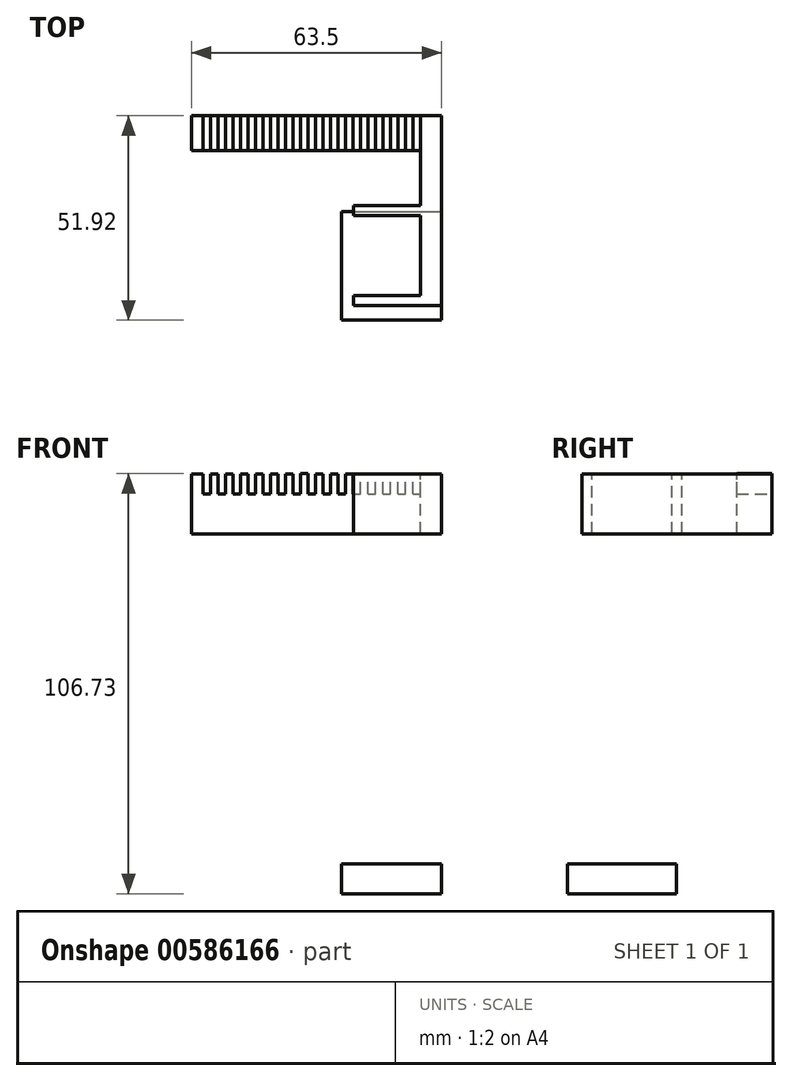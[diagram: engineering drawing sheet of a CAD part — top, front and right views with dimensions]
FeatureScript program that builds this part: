
annotation { "Feature Type Name" : "Feature", "Feature Type Description" : "" }
export const myFeature = defineFeature(function(context is Context, id is Id, definition is map)
    precondition{}
    {
        {
            var Q0;
            Q0=qCreatedBy(makeId("Front.planeOp"),FACE);
            var sketch = newSketch(context, id + "F0", { "sketchPlane" : qUnion([Q0])});
            skLineSegment(sketch, "E0.bottom", {"start": v(-64.89, 15.49) * mm, "end": v(-1.39, 15.49) * mm});
            skLineSegment(sketch, "E0.top", {"start": v(-64.89, 5.33) * mm, "end": v(-1.39, 5.33) * mm});
            skLineSegment(sketch, "E0.left", {"start": v(-64.89, 15.49) * mm, "end": v(-64.89, 5.33) * mm});
            skLineSegment(sketch, "E0.right", {"start": v(-1.39, 15.49) * mm, "end": v(-1.39, 5.33) * mm});
            skLineSegment(sketch, "E1.bottom", {"start": v(-1.39, 15.49) * mm, "end": v(-13.31, 15.49) * mm});
            skLineSegment(sketch, "E1.top", {"start": v(-11.73, 20.57) * mm, "end": v(-13.31, 20.57) * mm});
            skLineSegment(sketch, "E2.bottom", {"start": v(-48.7, 15.49) * mm, "end": v(-46.79, 15.49) * mm});
            skLineSegment(sketch, "E2.top", {"start": v(-48.7, 20.57) * mm, "end": v(-46.79, 20.57) * mm});
            skLineSegment(sketch, "E2.left", {"start": v(-48.7, 15.49) * mm, "end": v(-48.7, 20.57) * mm});
            skLineSegment(sketch, "E2.right", {"start": v(-46.79, 15.49) * mm, "end": v(-46.79, 20.57) * mm});
            skLineSegment(sketch, "E3.bottom", {"start": v(-44.88, 15.49) * mm, "end": v(-42.98, 15.49) * mm});
            skLineSegment(sketch, "E3.top", {"start": v(-44.88, 20.57) * mm, "end": v(-42.98, 20.57) * mm});
            skLineSegment(sketch, "E3.left", {"start": v(-44.88, 15.49) * mm, "end": v(-44.88, 20.57) * mm});
            skLineSegment(sketch, "E3.right", {"start": v(-42.98, 15.49) * mm, "end": v(-42.98, 20.57) * mm});
            skLineSegment(sketch, "E4.bottom", {"start": v(-41.07, 15.49) * mm, "end": v(-39.17, 15.49) * mm});
            skLineSegment(sketch, "E4.top", {"start": v(-41.07, 20.57) * mm, "end": v(-39.17, 20.57) * mm});
            skLineSegment(sketch, "E4.left", {"start": v(-41.07, 15.49) * mm, "end": v(-41.07, 20.57) * mm});
            skLineSegment(sketch, "E4.right", {"start": v(-39.17, 15.49) * mm, "end": v(-39.17, 20.57) * mm});
            skLineSegment(sketch, "E5.bottom", {"start": v(-37.26, 15.49) * mm, "end": v(-35.36, 15.49) * mm});
            skLineSegment(sketch, "E5.top", {"start": v(-37.26, 20.62) * mm, "end": v(-35.36, 20.62) * mm});
            skLineSegment(sketch, "E5.left", {"start": v(-37.26, 15.49) * mm, "end": v(-37.26, 20.62) * mm});
            skLineSegment(sketch, "E5.right", {"start": v(-35.36, 15.49) * mm, "end": v(-35.36, 20.62) * mm});
            skLineSegment(sketch, "E6.bottom", {"start": v(-33.45, 15.49) * mm, "end": v(-31.55, 15.49) * mm});
            skLineSegment(sketch, "E6.top", {"start": v(-33.45, 20.57) * mm, "end": v(-31.55, 20.57) * mm});
            skLineSegment(sketch, "E6.left", {"start": v(-33.45, 15.49) * mm, "end": v(-33.45, 20.57) * mm});
            skLineSegment(sketch, "E6.right", {"start": v(-31.55, 15.49) * mm, "end": v(-31.55, 20.57) * mm});
            skLineSegment(sketch, "E7.bottom", {"start": v(-29.64, 15.49) * mm, "end": v(-27.74, 15.49) * mm});
            skLineSegment(sketch, "E7.top", {"start": v(-29.64, 20.57) * mm, "end": v(-27.74, 20.57) * mm});
            skLineSegment(sketch, "E7.left", {"start": v(-29.64, 15.49) * mm, "end": v(-29.64, 20.57) * mm});
            skLineSegment(sketch, "E7.right", {"start": v(-27.74, 15.49) * mm, "end": v(-27.74, 20.57) * mm});
            skLineSegment(sketch, "E8.bottom", {"start": v(-25.83, 15.49) * mm, "end": v(-23.93, 15.49) * mm});
            skLineSegment(sketch, "E8.top", {"start": v(-25.83, 20.57) * mm, "end": v(-23.93, 20.57) * mm});
            skLineSegment(sketch, "E8.left", {"start": v(-25.83, 15.49) * mm, "end": v(-25.83, 20.57) * mm});
            skLineSegment(sketch, "E8.right", {"start": v(-23.93, 15.49) * mm, "end": v(-23.93, 20.57) * mm});
            skLineSegment(sketch, "E9.bottom", {"start": v(-22.02, 15.49) * mm, "end": v(-20.12, 15.49) * mm});
            skLineSegment(sketch, "E9.top", {"start": v(-22.02, 20.57) * mm, "end": v(-20.12, 20.57) * mm});
            skLineSegment(sketch, "E9.left", {"start": v(-22.02, 15.49) * mm, "end": v(-22.02, 20.57) * mm});
            skLineSegment(sketch, "E9.right", {"start": v(-20.12, 15.49) * mm, "end": v(-20.12, 20.57) * mm});
            skLineSegment(sketch, "E10.bottom", {"start": v(-18.21, 15.49) * mm, "end": v(-16.3, 15.49) * mm});
            skLineSegment(sketch, "E10.top", {"start": v(-18.21, 20.57) * mm, "end": v(-16.3, 20.57) * mm});
            skLineSegment(sketch, "E10.left", {"start": v(-18.21, 15.49) * mm, "end": v(-18.21, 20.57) * mm});
            skLineSegment(sketch, "E10.right", {"start": v(-16.3, 15.49) * mm, "end": v(-16.3, 20.57) * mm});
            skLineSegment(sketch, "E11.bottom", {"start": v(-8.69, 15.49) * mm, "end": v(-10.6, 15.49) * mm});
            skLineSegment(sketch, "E11.top", {"start": v(-8.69, 20.57) * mm, "end": v(-10.6, 20.57) * mm});
            skLineSegment(sketch, "E11.left", {"start": v(-8.69, 15.49) * mm, "end": v(-8.69, 20.57) * mm});
            skLineSegment(sketch, "E11.right", {"start": v(-10.6, 15.49) * mm, "end": v(-10.6, 20.57) * mm});
            skLineSegment(sketch, "E12.bottom", {"start": v(-14.4, 15.49) * mm, "end": v(-12.5, 15.49) * mm});
            skLineSegment(sketch, "E12.top", {"start": v(-14.4, 20.57) * mm, "end": v(-12.5, 20.57) * mm});
            skLineSegment(sketch, "E12.left", {"start": v(-14.4, 15.49) * mm, "end": v(-14.4, 20.57) * mm});
            skLineSegment(sketch, "E12.right", {"start": v(-12.5, 15.49) * mm, "end": v(-12.5, 20.57) * mm});
            skLineSegment(sketch, "E13.bottom", {"start": v(-6.78, 15.49) * mm, "end": v(-1.39, 15.49) * mm});
            skLineSegment(sketch, "E13.top", {"start": v(-6.78, 20.57) * mm, "end": v(-1.39, 20.57) * mm});
            skLineSegment(sketch, "E13.left", {"start": v(-6.78, 15.49) * mm, "end": v(-6.78, 20.57) * mm});
            skLineSegment(sketch, "E13.right", {"start": v(-1.39, 15.49) * mm, "end": v(-1.39, 20.57) * mm});
            skLineSegment(sketch, "E14.bottom", {"start": v(-50.6, 15.49) * mm, "end": v(-52.5, 15.49) * mm});
            skLineSegment(sketch, "E14.top", {"start": v(-50.6, 20.57) * mm, "end": v(-52.5, 20.57) * mm});
            skLineSegment(sketch, "E14.left", {"start": v(-50.6, 15.49) * mm, "end": v(-50.6, 20.57) * mm});
            skLineSegment(sketch, "E14.right", {"start": v(-52.5, 15.49) * mm, "end": v(-52.5, 20.57) * mm});
            skLineSegment(sketch, "E15.bottom", {"start": v(-54.4, 15.49) * mm, "end": v(-56.31, 15.49) * mm});
            skLineSegment(sketch, "E15.top", {"start": v(-54.4, 20.57) * mm, "end": v(-56.31, 20.57) * mm});
            skLineSegment(sketch, "E15.left", {"start": v(-54.4, 15.49) * mm, "end": v(-54.4, 20.57) * mm});
            skLineSegment(sketch, "E15.right", {"start": v(-56.31, 15.49) * mm, "end": v(-56.31, 20.57) * mm});
            skLineSegment(sketch, "E16.bottom", {"start": v(-58.22, 15.49) * mm, "end": v(-60.12, 15.49) * mm});
            skLineSegment(sketch, "E16.top", {"start": v(-58.22, 20.57) * mm, "end": v(-60.12, 20.57) * mm});
            skLineSegment(sketch, "E16.left", {"start": v(-58.22, 15.49) * mm, "end": v(-58.22, 20.57) * mm});
            skLineSegment(sketch, "E16.right", {"start": v(-60.12, 15.49) * mm, "end": v(-60.12, 20.57) * mm});
            skLineSegment(sketch, "E17.bottom", {"start": v(-64.89, 15.49) * mm, "end": v(-62.03, 15.49) * mm});
            skLineSegment(sketch, "E17.top", {"start": v(-64.89, 20.57) * mm, "end": v(-62.03, 20.57) * mm});
            skLineSegment(sketch, "E17.left", {"start": v(-64.89, 15.49) * mm, "end": v(-64.89, 20.57) * mm});
            skLineSegment(sketch, "E17.right", {"start": v(-62.03, 15.49) * mm, "end": v(-62.03, 20.57) * mm});
            skSolve(sketch);
        }
        {
            var Q0;
            Q0=qSketchRegion(id+"F0",true);
            extrude(context, id + "F1", {"entities" : qUnion([Q0]), "endBound" : BoundingType.SYMMETRIC, "depth" : 8.9 * mm, "offsetDistance" : 25.4 * mm});
        }
        {
            var Q0;
            Q0=makeQuery(id+"F1.opExtrude","SWEPT_FACE",FACE,{"disambiguationData":[OSD([sQuery(id+"F0.wireOp",EDGE,"E0.right"),sQuery(id+"F0.wireOp",EDGE,"E13.right")])]});
            var sketch = newSketch(context, id + "F2", { "sketchPlane" : qUnion([Q0])});
            skLineSegment(sketch, "E18.bottom", {"start": v(-4.45, 20.57) * mm, "end": v(-43.82, 20.57) * mm});
            skLineSegment(sketch, "E18.top", {"start": v(-4.45, 5.33) * mm, "end": v(-43.82, 5.33) * mm});
            skLineSegment(sketch, "E18.left", {"start": v(-4.45, 20.57) * mm, "end": v(-4.45, 5.33) * mm});
            skLineSegment(sketch, "E18.right", {"start": v(-43.82, 20.57) * mm, "end": v(-43.82, 5.33) * mm});
            skLineSegment(sketch, "E19.bottom", {"start": v(-37.47, 5.33) * mm, "end": v(-29.84, 5.33) * mm});
            skLineSegment(sketch, "E19.top", {"start": v(-37.46, -78.5) * mm, "end": v(-29.84, -78.5) * mm});
            skLineSegment(sketch, "E19.left", {"start": v(-37.47, 5.33) * mm, "end": v(-37.46, -78.5) * mm});
            skLineSegment(sketch, "E19.right", {"start": v(-29.85, 5.33) * mm, "end": v(-29.84, -78.5) * mm});
            skPoint(sketch, "E20.middle", {"position": v(-33.65, -78.5) * mm});
            skLineSegment(sketch, "E21.bottom", {"start": v(-19.84, -78.5) * mm, "end": v(-47.47, -78.5) * mm});
            skLineSegment(sketch, "E21.top", {"start": v(-19.84, -86.11) * mm, "end": v(-47.47, -86.11) * mm});
            skLineSegment(sketch, "E21.left", {"start": v(-19.84, -78.5) * mm, "end": v(-19.84, -86.11) * mm});
            skLineSegment(sketch, "E21.right", {"start": v(-47.47, -78.5) * mm, "end": v(-47.47, -86.11) * mm});
            skPoint(sketch, "E21.middle", {"position": v(-33.65, -82.3) * mm});
            skSolve(sketch);
        }
        {
            var Q0;
            Q0=makeQuery(id+"F2.imprint","IMPRINT",FACE,{"disambiguationData":[TD([[makeQuery(id+"F2.imprint","IMPRINT",EDGE,{"derivedFrom":sQuery(id+"F2.wireOp",EDGE,"E18.bottom")}),1.0]])]});
            var Q1;
            {var subQ0=sQuery(id+"F2.wireOp",EDGE,"E19.bottom");Q1=makeQuery(id+"F2.imprint","IMPRINT",FACE,{"disambiguationData":[TD([[makeQuery(id+"F2.imprint","IMPRINT",EDGE,{"derivedFrom":subQ0}),-1.0]])]});}
            extrude(context, id + "F3", {"entities" : qUnion([Q0, Q1]), "operationType" : NewBodyOperationType.ADD, "oppositeDirection" : true, "depth" : 5.4 * mm, "offsetDistance" : 25.4 * mm});
        }
        {
            var Q0;
            Q0=makeQuery(id+"F3.boolean.opBoolean","MERGE",FACE,{"derivedFrom":[makeQuery(id+"F1.opExtrude","SWEPT_FACE",FACE,{"disambiguationData":[OSD([sQuery(id+"F0.wireOp",EDGE,"E13.top")])]}),makeQuery(id+"F3.opExtrude","SWEPT_FACE",FACE,{"disambiguationData":[OSD([sQuery(id+"F2.wireOp",EDGE,"E18.bottom")])]})]});
            var sketch = newSketch(context, id + "F4", { "sketchPlane" : qUnion([Q0])});
            skLineSegment(sketch, "E22.bottom", {"start": v(-6.78, -43.82) * mm, "end": v(-23.8, -43.82) * mm});
            skLineSegment(sketch, "E22.top", {"start": v(-6.78, -41.28) * mm, "end": v(-23.8, -41.28) * mm});
            skLineSegment(sketch, "E22.left", {"start": v(-6.78, -43.82) * mm, "end": v(-6.78, -41.28) * mm});
            skLineSegment(sketch, "E22.right", {"start": v(-23.8, -43.82) * mm, "end": v(-23.8, -41.28) * mm});
            skLineSegment(sketch, "E23.bottom", {"start": v(-6.78, -20.96) * mm, "end": v(-23.8, -20.96) * mm});
            skLineSegment(sketch, "E23.top", {"start": v(-6.78, -18.42) * mm, "end": v(-23.8, -18.42) * mm});
            skLineSegment(sketch, "E23.left", {"start": v(-6.78, -20.96) * mm, "end": v(-6.78, -18.42) * mm});
            skLineSegment(sketch, "E23.right", {"start": v(-23.8, -20.96) * mm, "end": v(-23.8, -18.42) * mm});
            skLineSegment(sketch, "E24.bottom", {"start": v(-23.8, -41.28) * mm, "end": v(-21.35, -41.28) * mm});
            skLineSegment(sketch, "E24.top", {"start": v(-23.8, -47) * mm, "end": v(-21.35, -47) * mm});
            skLineSegment(sketch, "E24.left", {"start": v(-23.8, -47) * mm, "end": v(-23.8, -41.28) * mm});
            skLineSegment(sketch, "E24.right", {"start": v(-21.35, -47) * mm, "end": v(-21.35, -41.28) * mm});
            skSolve(sketch);
        }
        {
            var Q0;
            Q0=makeQuery(id+"F4.imprint","IMPRINT",FACE,{"disambiguationData":[TD([[makeQuery(id+"F4.imprint","IMPRINT",EDGE,{"derivedFrom":sQuery(id+"F4.wireOp",EDGE,"u9V1ZfCU-yo13-MF0e-S9b7-lnSjsBYDx5Rl.bottom")}),-1.0]])]});
            var Q1;
            Q1=makeQuery(id+"F4.imprint","IMPRINT",FACE,{"disambiguationData":[TD([[makeQuery(id+"F4.imprint","IMPRINT",EDGE,{"derivedFrom":sQuery(id+"F4.wireOp",EDGE,"E23.bottom")}),-1.0]])]});
            var Q2;
            Q2=makeQuery(id+"F4.imprint","IMPRINT",FACE,{"disambiguationData":[TD([[makeQuery(id+"F4.imprint","IMPRINT",EDGE,{"derivedFrom":sQuery(id+"F4.wireOp",EDGE,"E24.bottom")}),1.0]])]});
            var Q3;
            Q3=makeQuery(id+"F4.imprint","IMPRINT",FACE,{"disambiguationData":[TD([[makeQuery(id+"F4.imprint","IMPRINT",EDGE,{"derivedFrom":sQuery(id+"F4.wireOp",EDGE,"E22.bottom")}),-1.0]])]});
            extrude(context, id + "F5", {"entities" : qUnion([Q0, Q1, Q2, Q3]), "operationType" : NewBodyOperationType.ADD, "oppositeDirection" : true, "depth" : 15.24 * mm, "offsetDistance" : 25.4 * mm});
        }
        {
            var Q0;
            Q0=makeQuery(id+"F2.imprint","IMPRINT",FACE,{"disambiguationData":[TD([[makeQuery(id+"F2.imprint","IMPRINT",EDGE,{"derivedFrom":sQuery(id+"F2.wireOp",EDGE,"E21.top")}),-1.0]])]});
            extrude(context, id + "F6", {"entities" : qUnion([Q0]), "oppositeDirection" : true, "depth" : 25.4 * mm, "offsetDistance" : 25.4 * mm});
        }
    });
